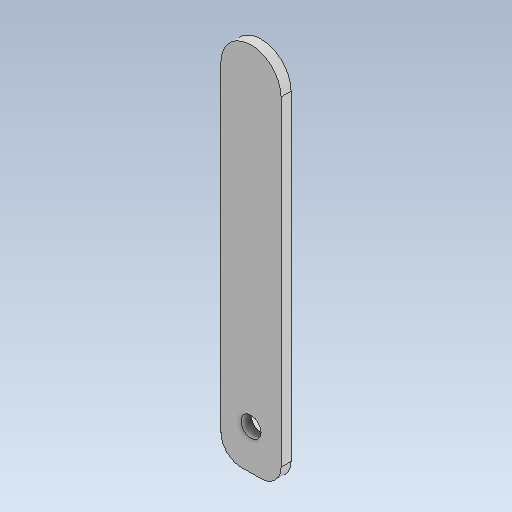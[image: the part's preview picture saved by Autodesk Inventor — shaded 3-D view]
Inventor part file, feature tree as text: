
AUTODESK INVENTOR PART (.ipt)
format: ipt  version: 2021 (Build 250183000, 183)  size: 106,496 bytes
history: native  units: mm
features: other x1, extrude x1, sketch x1
ambient origin geometry x8: Origin, YZ Plane, XZ Plane, XY Plane, X Axis, Y Axis, Z Axis, Center Point
bodies: Body1 (feature_tree)
feature tree (3):
  other  "Sólido1"
  extrude  "Extrusión1"  Depth=2.0mm
  sketch  "Boceto1"  dims[d2=4.0mm d3=2.0mm d4=1.0mm d5=0.0mm d6=2.0mm d7=6.0mm d8=37.0mm]
